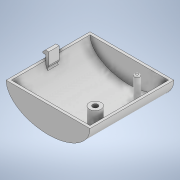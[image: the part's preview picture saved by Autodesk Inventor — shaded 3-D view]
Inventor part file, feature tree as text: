
AUTODESK INVENTOR PART (.ipt)
format: ipt  version: 2021 (Build 250183000, 183)  size: 249,856 bytes
history: native  units: mm
features: sketch x9, extrude x8, fillet x2, other x1, shell x1, plane x1, hole x1, thread x1
ambient origin geometry x8: Origin, YZ Plane, XZ Plane, XY Plane, X Axis, Y Axis, Z Axis, Center Point
bodies: Body1 (feature_tree)
feature tree (24):
  other  "Sólido1"
  sketch  "Boceto1"  dims[d0=2.5mm d2=3.0mm d3=4.0mm]
  extrude  "Extrusión1"  Depth=3.0mm
  shell  "Vaciado1"  Thickness=4.0mm
  plane  "Plano de trabajo2"
  extrude  "Extrusión2"  Depth=2.0mm
  extrude  "Extrusión3"  Depth=30.0mm
  extrude  "Extrusión4"  Depth=20.0mm TaperAngle=0.0deg
  extrude  "Extrusión5"  Depth=2.0mm TaperAngle=0.0deg
  fillet  "Empalme1"  [1 undecoded]
  extrude  "Extrusión6"  Depth=10.0mm
  hole  "Agujero1"  [1 undecoded]
  thread  "Rosca1"  [1 undecoded]
  extrude  "Extrusión7"  Depth=30.0mm
  extrude  "Extrusión8"  Depth=2.0mm
  fillet  "Empalme2"  Radius=1.0mm
  sketch  "Boceto2"  dims[d4=4.0mm d6=2.0mm]
  sketch  "Boceto3"  dims[d7=30.0mm d8=64.0mm]
  sketch  "Boceto4"  dims[d9=64.0mm d10=20.0mm d11=0.0mm]
  sketch  "Boceto5"  dims[d12=2.0mm d13=20.0mm d14=0.0mm d19=-20.0mm]
  sketch  "Boceto6"  dims[d20=10.0mm d21=16.0mm]
  sketch  "Boceto7"  dims[d22=16.0mm d23=4.0mm d24=9.0mm]
  sketch  "Boceto8"  dims[d25=30.0mm d26=0.0mm d27=0.25mm]
  sketch  "Boceto9"  dims[d28=45.0deg d29=2.0mm d30=1.0mm d31=3.0mm d32=45.0deg d33=2.0mm d34=5.0mm d35=4.0mm d36=0.0mm d37=0.0mm d38=8.0mm d39=0.0mm d40=4.0mm d41=6.0mm d42=0.0mm d43=1.0mm d44=9.0mm d45=1.0mm d46=0.0mm d47=4.0mm d48=4.0mm d49=6.0mm d50=4.0mm d51=2.0mm d52=90.0deg d53=10.0mm d54=0.0mm d55=10.0mm d56=0.0mm d59=20.0mm d60=15.0mm d61=1.0mm d62=0.0mm d63=20.0mm d65=0.0mm d66=0.0mm d67=2.0mm]
note: 3 required parameter values undecoded (feature->parameter linkage not recoverable at this tier; creation-order binding heuristic only, values carry confidence <= 0.55)
